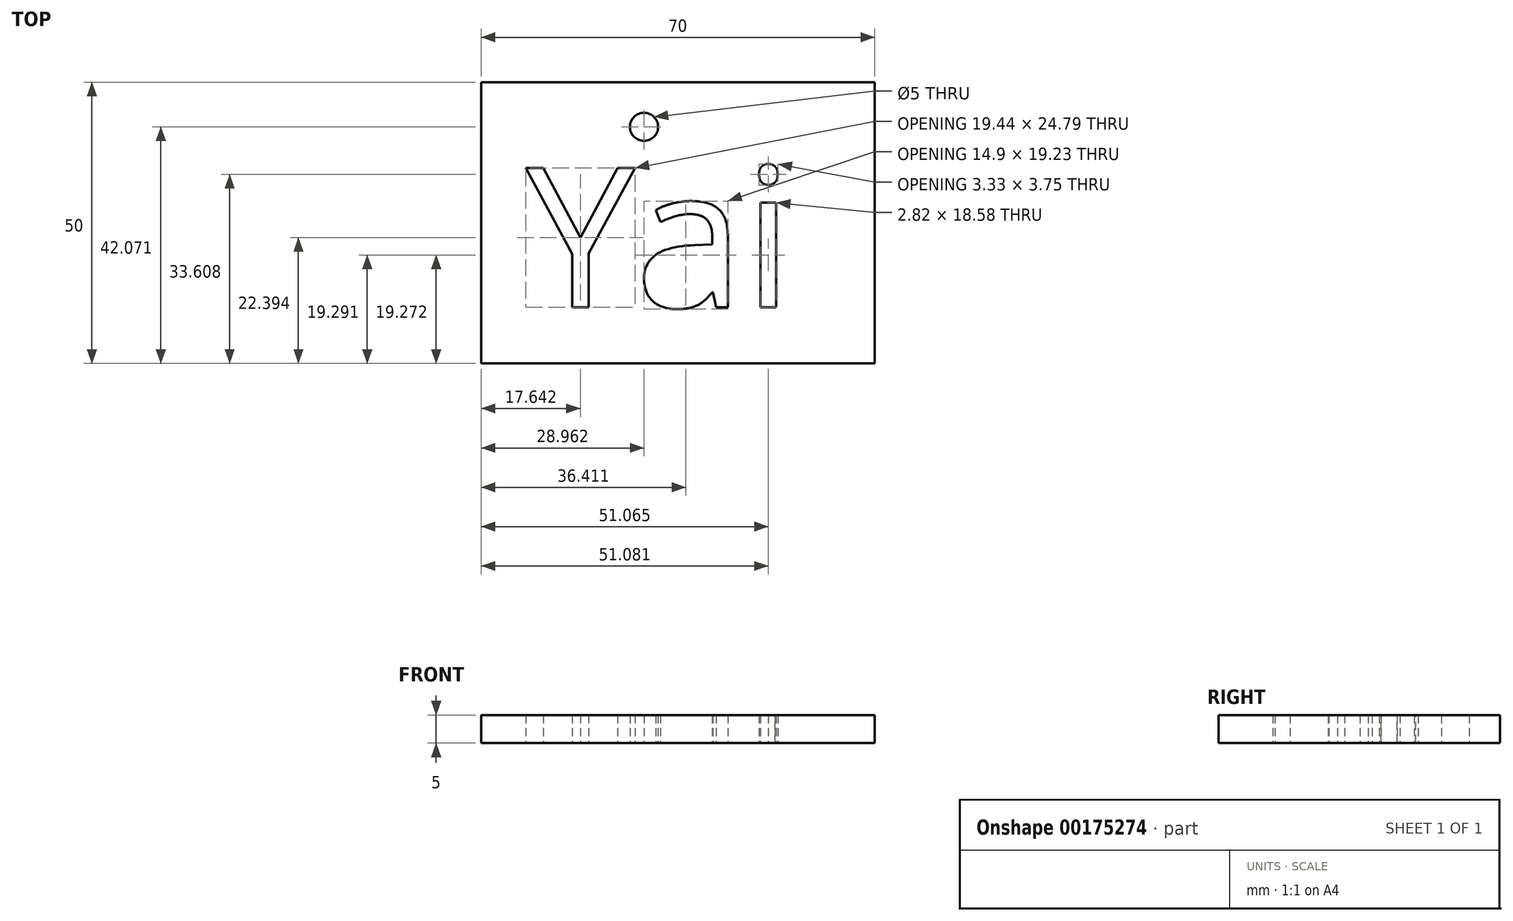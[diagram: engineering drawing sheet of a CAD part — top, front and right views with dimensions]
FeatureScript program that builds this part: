
annotation { "Feature Type Name" : "Feature", "Feature Type Description" : "" }
export const myFeature = defineFeature(function(context is Context, id is Id, definition is map)
    precondition{}
    {
        {
            var Q0;
            Q0=qCreatedBy(makeId("Top.planeOp"),FACE);
            var sketch = newSketch(context, id + "F0", { "sketchPlane" : qUnion([Q0])});
            skLineSegment(sketch, "E0.bottom", {"start": v(-70, 50) * mm, "end": v(0, 50) * mm});
            skLineSegment(sketch, "E0.top", {"start": v(-70, 0) * mm, "end": v(0, 0) * mm});
            skLineSegment(sketch, "E0.left", {"start": v(-70, 50) * mm, "end": v(-70, 0) * mm});
            skLineSegment(sketch, "E0.right", {"start": v(0, 50) * mm, "end": v(0, 0) * mm});
            skText(sketch, "E1", { "text": "Yai", "fontName": "OpenSans-Regular.ttf"});
            skCircle(sketch, "E2", {"center": v(-41.04, 42.07) * mm, "radius": 2.5 * mm});
            const initialGuessF0  = {"E1": [-0.06208, 0.01, 1, 0, 0.025]};
            skSetInitialGuess(sketch, initialGuessF0);
            skSolve(sketch);
        }
        {
            var Q0;
            Q0 = qSketchRegion(id + "F0", true);
            extrude(context, id + "F1", {"entities" : qUnion([Q0]), "depth" : 5 * mm});
        }
    });
